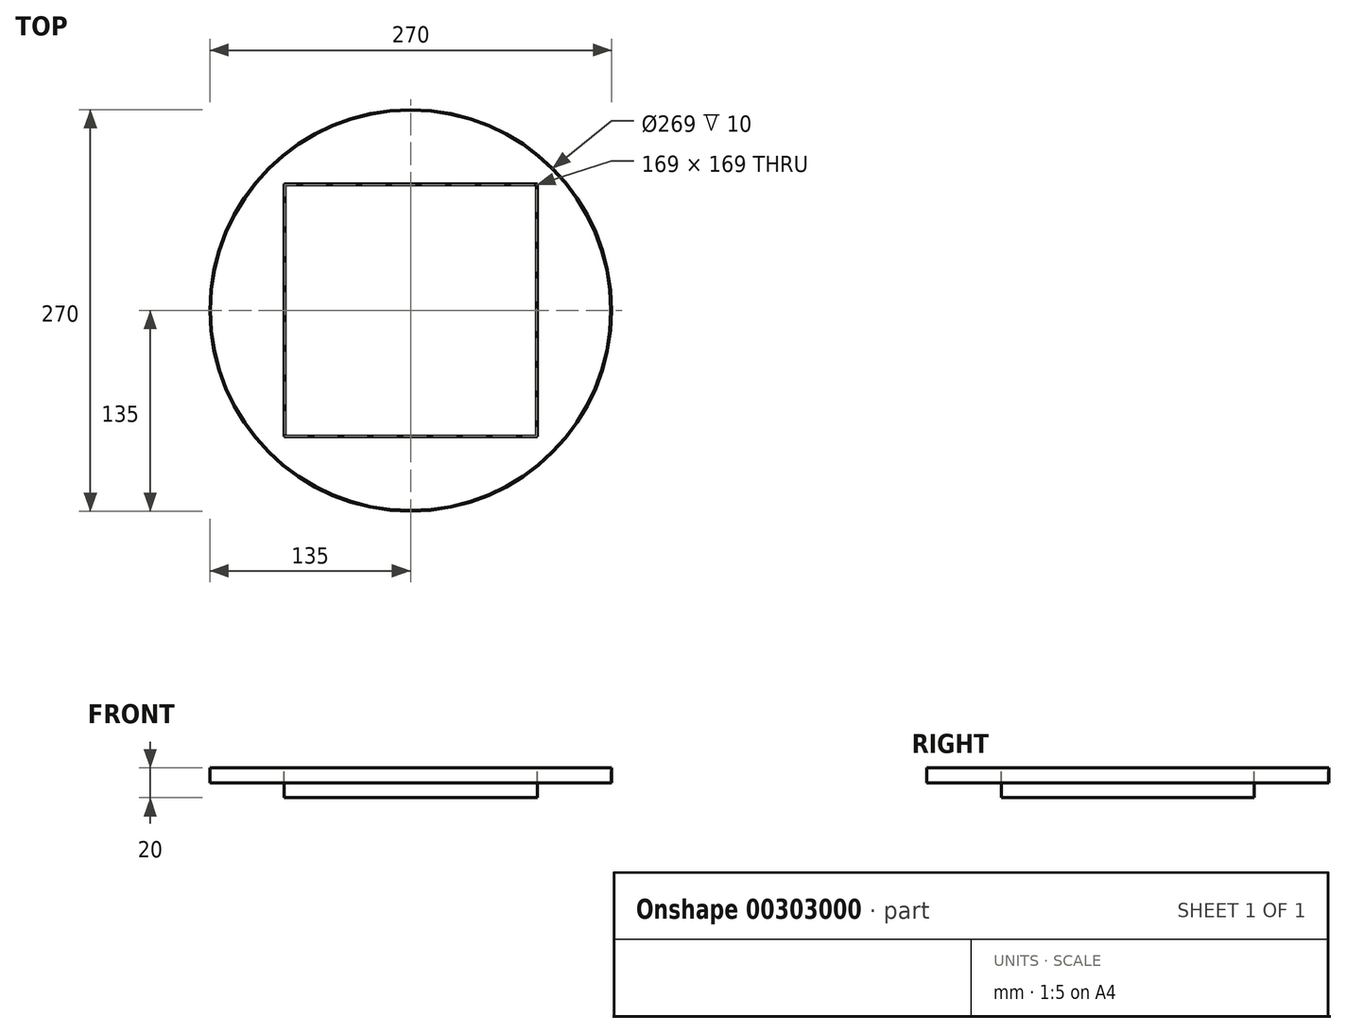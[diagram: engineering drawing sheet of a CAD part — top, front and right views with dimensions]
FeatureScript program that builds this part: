
annotation { "Feature Type Name" : "Feature", "Feature Type Description" : "" }
export const myFeature = defineFeature(function(context is Context, id is Id, definition is map)
    precondition{}
    {
        {
            var Q0;
            Q0=qCreatedBy(makeId("Top.planeOp"),FACE);
            var sketch = newSketch(context, id + "F0", { "sketchPlane" : qUnion([Q0])});
            skCircle(sketch, "E0", {"center": v(0, 0) * mm, "radius": 75 * mm});
            skCircle(sketch, "E1", {"center": v(0, 0) * mm, "radius": 134.5 * mm});
            skCircle(sketch, "E2", {"center": v(0, 0) * mm, "radius": 50 * mm});
            skCircle(sketch, "E3", {"center": v(0, 0) * mm, "radius": 72.5 * mm});
            skCircle(sketch, "E4", {"center": v(0, 0) * mm, "radius": 47.5 * mm});
            skCircle(sketch, "E5", {"center": v(0, 0) * mm, "radius": 135 * mm});
            skLineSegment(sketch, "E6.bottom", {"start": v(-85, 85) * mm, "end": v(85, 85) * mm});
            skLineSegment(sketch, "E6.top", {"start": v(-85, -85) * mm, "end": v(85, -85) * mm});
            skLineSegment(sketch, "E6.left", {"start": v(-85, 85) * mm, "end": v(-85, -85) * mm});
            skLineSegment(sketch, "E6.right", {"start": v(85, 85) * mm, "end": v(85, -85) * mm});
            skLineSegment(sketch, "E7.bottom", {"start": v(-84.5, 84.5) * mm, "end": v(84.5, 84.5) * mm});
            skLineSegment(sketch, "E7.top", {"start": v(-84.5, -84.5) * mm, "end": v(84.5, -84.5) * mm});
            skLineSegment(sketch, "E7.left", {"start": v(-84.5, 84.5) * mm, "end": v(-84.5, -84.5) * mm});
            skLineSegment(sketch, "E7.right", {"start": v(84.5, 84.5) * mm, "end": v(84.5, -84.5) * mm});
            skSolve(sketch);
        }
        {
            var Q0;
            Q0=makeQuery(id+"F0.imprint","IMPRINT",FACE,{"disambiguationData":[TD([[makeQuery(id+"F0.imprint","IMPRINT",EDGE,{"derivedFrom":sQuery(id+"F0.wireOp",EDGE,"E1")}),-1.0]])]});
            extrude(context, id + "F1", {"entities" : qUnion([Q0]), "oppositeDirection" : true, "depth" : 10 * mm, "offsetDistance" : 25 * mm});
        }
        {
            var Q0;
            Q0=makeQuery(id+"F0.imprint","IMPRINT",FACE,{"disambiguationData":[TD([[makeQuery(id+"F0.imprint","IMPRINT",EDGE,{"derivedFrom":sQuery(id+"F0.wireOp",EDGE,"E6.bottom")}),-1.0]])]});
            extrude(context, id + "F2", {"entities" : qUnion([Q0]), "oppositeDirection" : true, "depth" : 20 * mm, "offsetDistance" : 25 * mm});
        }
    });
